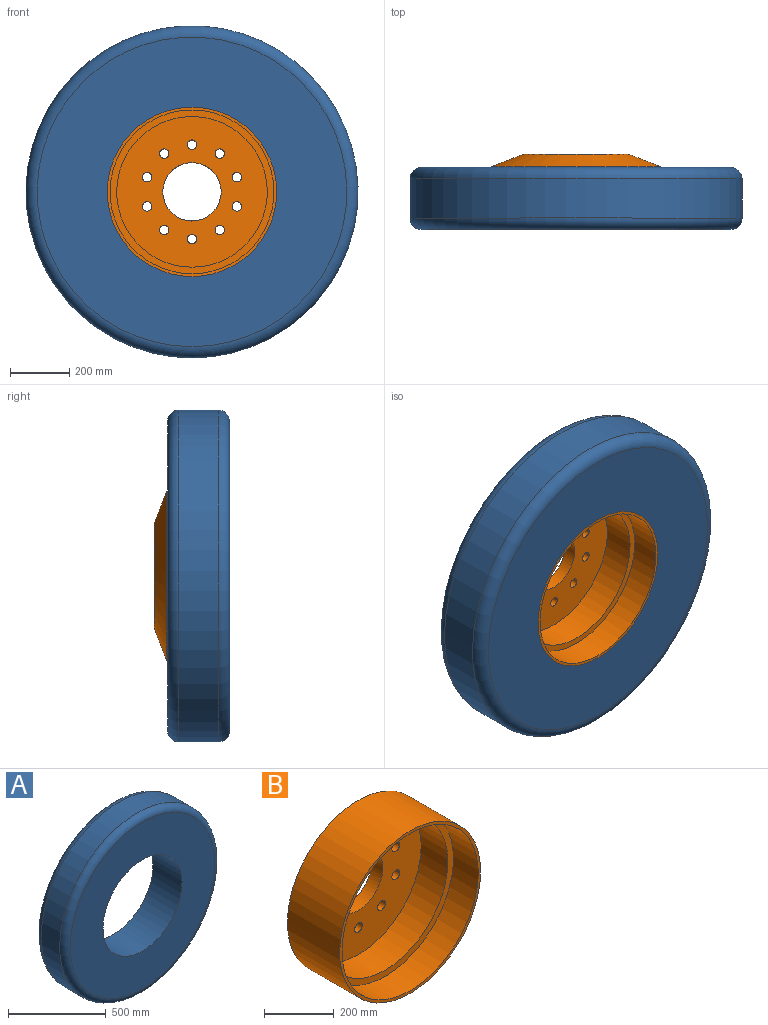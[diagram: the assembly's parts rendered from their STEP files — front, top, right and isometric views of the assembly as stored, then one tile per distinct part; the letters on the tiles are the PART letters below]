
ASSEMBLY  parts=2 mates=1
PART A: 6 faces, bbox 1212.4x209.6x1212.4 mm
  f0: cylinder r=285.75mm len=571.5mm, axis (0,1,0), area 376230.3mm2, adj f2,f3
  f1: cylinder r=560.07mm len=1120.14mm, axis (0,1,0), area 469261.8mm2, adj f4,f5
  f2: plane 1043.94x1043.94mm, normal (0,-1,0), area 599414.7mm2, adj f0,f5
  f3: plane 1043.94x1043.94mm, normal (0,1,0), area 599414.7mm2, adj f0,f4
  f4: torus R=521.97mm, axis (0,-1,0), area 205398.1mm2, adj f1,f3
  f5: torus R=521.97mm, axis (0,-1,0), area 205398.1mm2, adj f1,f2
PART B: 19 faces, bbox 571.5x254x571.5 mm
  f0: cylinder r=254mm len=508mm, axis (0,-1,0), area 173496.6mm2, adj f3,f8
  f1: cylinder r=285.75mm len=571.5mm, axis (0,1,0), area 380775.4mm2, adj f2,f4
  f2: plane 571.5x571.5mm, normal (0,-1,0), area 16816.4mm2, adj f1,f7
  f3: plane 508x508mm, normal (0,-1,0), area 164331.6mm2, adj f0,f6,f9,f10,f11,f12,f13,f14
  f4: cone r=177.8mm half-angle=68.8deg, axis (0,-1,0), area 168642.4mm2, adj f1,f5
  f5: plane 355.6x355.6mm, normal (0,1,0), area 60963.2mm2, adj f4,f6,f9,f10,f11,f12,f13,f14
  f6: cylinder r=98.42mm len=196.85mm, axis (0,1,0), area 27488.9mm2, adj f3,f5
  f7: cylinder r=276.23mm len=552.45mm, axis (0,-1,0), area 175011.7mm2, adj f2,f8
  f8: plane 552.45x552.45mm, normal (0,-1,0), area 37021.3mm2, adj f0,f7
  f9: cylinder r=15.88mm len=44.45mm, axis (0,-1,0), area 4433.7mm2, adj f3,f5
  f10: cylinder r=15.88mm len=44.45mm, axis (0,-1,0), area 4433.7mm2, adj f3,f5
  f11: cylinder r=15.88mm len=44.45mm, axis (0,-1,0), area 4433.7mm2, adj f3,f5
  f12: cylinder r=15.88mm len=44.45mm, axis (0,-1,0), area 4433.7mm2, adj f3,f5
  f13: cylinder r=15.88mm len=44.45mm, axis (0,-1,0), area 4433.7mm2, adj f3,f5
  f14: cylinder r=15.88mm len=44.45mm, axis (0,-1,0), area 4433.7mm2, adj f3,f5
  f15: cylinder r=15.88mm len=44.45mm, axis (0,-1,0), area 4433.7mm2, adj f3,f5
  f16: cylinder r=15.88mm len=44.45mm, axis (0,-1,0), area 4433.7mm2, adj f3,f5
  f17: cylinder r=15.88mm len=44.45mm, axis (0,-1,0), area 4433.7mm2, adj f3,f5
  f18: cylinder r=15.88mm len=44.45mm, axis (0,-1,0), area 4433.7mm2, adj f3,f5
PLACE A t=(-154.66,-24.05,-25.96)mm
PLACE B t=(-154.66,20.4,-25.96)mm
MATE fastened A.f1 <-> B.f7  axis (0,-1,0) through (-154.66,-233.6,-25.96)mm
